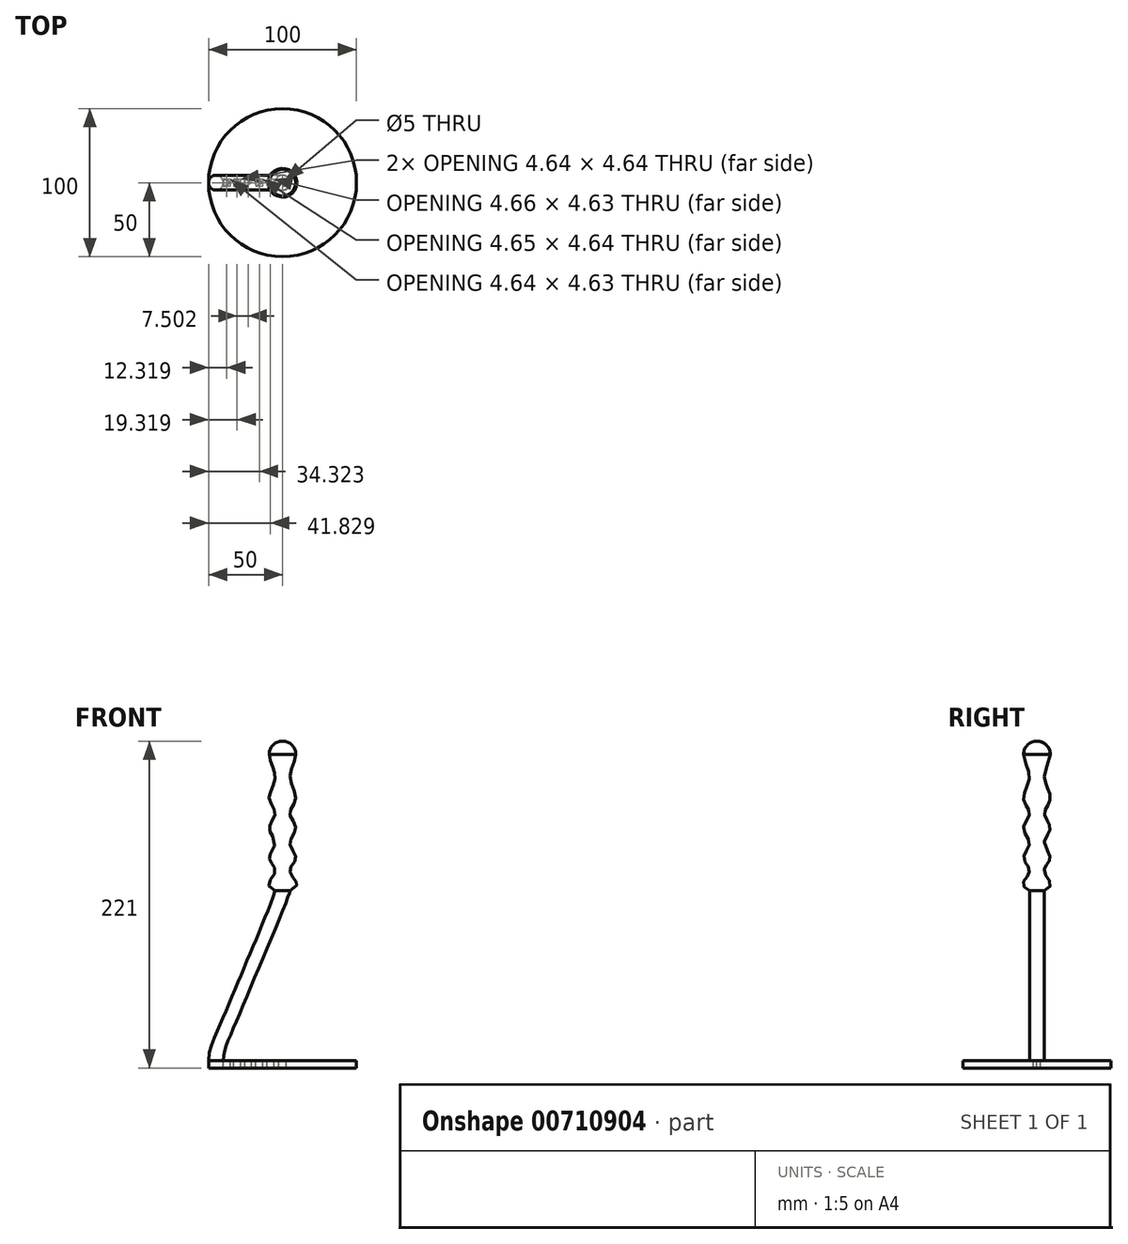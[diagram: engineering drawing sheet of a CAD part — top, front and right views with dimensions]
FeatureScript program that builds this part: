
annotation { "Feature Type Name" : "Feature", "Feature Type Description" : "" }
export const myFeature = defineFeature(function(context is Context, id is Id, definition is map)
    precondition{}
    {
        {
            var Q0;
            Q0=qCreatedBy(makeId("Top.planeOp"),FACE);
            var sketch = newSketch(context, id + "F0", { "sketchPlane" : qUnion([Q0])});
            skCircle(sketch, "E0", {"center": v(0, 0) * mm, "radius": 50 * mm});
            skLineSegment(sketch, "E1", {"start": v(0, 0) * mm, "end": v(-50, 0) * mm, "construction": true});
            skLineSegment(sketch, "E2", {"start": v(-50, 0) * mm, "end": v(-45, 0) * mm, "construction": true});
            skCircle(sketch, "E3", {"center": v(-45, 0) * mm, "radius": 5 * mm});
            skCircle(sketch, "E4", {"center": v(0, 0) * mm, "radius": 40 * mm, "construction": true});
            skLineSegment(sketch, "E5", {"start": v(-39.5, -2.29) * mm, "end": v(-35.53, -0.27) * mm});
            skLineSegment(sketch, "E6", {"start": v(-35.53, 0.27) * mm, "end": v(-39.5, 2.29) * mm});
            skLineSegment(sketch, "E7", {"start": v(-39.94, 2.03) * mm, "end": v(-40, 0) * mm});
            skLineSegment(sketch, "E8", {"start": v(-40, 0) * mm, "end": v(-39.94, -2.03) * mm});
            skPoint(sketch, "E9.visualSharp", {"position": v(-39.92, 2.5) * mm});
            skArc(sketch, "E9.filletArc", {"start": v(-39.5, 2.29) * mm, "mid": v(-39.79, 2.28) * mm, "end": v(-39.94, 2.03) * mm});
            skPoint(sketch, "E10.visualSharp", {"position": v(-35, 0) * mm});
            skArc(sketch, "E10.filletArc", {"start": v(-35.53, -0.27) * mm, "mid": v(-35.36, 0) * mm, "end": v(-35.53, 0.27) * mm});
            skPoint(sketch, "E11.visualSharp", {"position": v(-39.92, -2.5) * mm});
            skArc(sketch, "E11.filletArc", {"start": v(-39.94, -2.03) * mm, "mid": v(-39.79, -2.28) * mm, "end": v(-39.5, -2.29) * mm});
            skLineSegment(sketch, "E12", {"start": v(-35, 0) * mm, "end": v(-33, 0) * mm, "construction": true});
            skCircle(sketch, "E13", {"center": v(0, 0) * mm, "radius": 33 * mm, "construction": true});
            skLineSegment(sketch, "E14", {"start": v(-33, 0) * mm, "end": v(-32.92, 2.03) * mm});
            skLineSegment(sketch, "E15", {"start": v(-32.49, 2.29) * mm, "end": v(-28.52, 0.27) * mm});
            skLineSegment(sketch, "E16", {"start": v(-28.52, -0.27) * mm, "end": v(-32.49, -2.29) * mm});
            skLineSegment(sketch, "E17", {"start": v(-32.92, -2.03) * mm, "end": v(-33, 0) * mm});
            skPoint(sketch, "E18.visualSharp", {"position": v(-28, 0) * mm});
            skArc(sketch, "E18.filletArc", {"start": v(-28.52, -0.27) * mm, "mid": v(-28.36, 0) * mm, "end": v(-28.52, 0.27) * mm});
            skPoint(sketch, "E19.visualSharp", {"position": v(-32.9, 2.5) * mm});
            skArc(sketch, "E19.filletArc", {"start": v(-32.49, 2.29) * mm, "mid": v(-32.78, 2.28) * mm, "end": v(-32.92, 2.03) * mm});
            skPoint(sketch, "E20.visualSharp", {"position": v(-32.9, -2.5) * mm});
            skArc(sketch, "E20.filletArc", {"start": v(-32.92, -2.03) * mm, "mid": v(-32.78, -2.28) * mm, "end": v(-32.49, -2.29) * mm});
            skLineSegment(sketch, "E21", {"start": v(-28, 0) * mm, "end": v(-25.5, 0) * mm, "construction": true});
            skCircle(sketch, "E22", {"center": v(0, 0) * mm, "radius": 25.5 * mm, "construction": true});
            skLineSegment(sketch, "E23", {"start": v(-25.5, 0) * mm, "end": v(-25.4, -2.03) * mm});
            skLineSegment(sketch, "E24", {"start": v(-24.96, -2.29) * mm, "end": v(-21.02, -0.27) * mm});
            skLineSegment(sketch, "E25", {"start": v(-21.02, 0.27) * mm, "end": v(-24.96, 2.29) * mm});
            skLineSegment(sketch, "E26", {"start": v(-25.4, 2.03) * mm, "end": v(-25.5, 0) * mm});
            skPoint(sketch, "E27.visualSharp", {"position": v(-25.38, -2.5) * mm});
            skArc(sketch, "E27.filletArc", {"start": v(-25.4, -2.03) * mm, "mid": v(-25.25, -2.28) * mm, "end": v(-24.96, -2.29) * mm});
            skPoint(sketch, "E28.visualSharp", {"position": v(-25.38, 2.5) * mm});
            skArc(sketch, "E28.filletArc", {"start": v(-24.96, 2.29) * mm, "mid": v(-25.25, 2.28) * mm, "end": v(-25.4, 2.03) * mm});
            skPoint(sketch, "E29.visualSharp", {"position": v(-20.5, 0) * mm});
            skArc(sketch, "E29.filletArc", {"start": v(-21.02, -0.27) * mm, "mid": v(-20.86, 0) * mm, "end": v(-21.02, 0.27) * mm});
            skLineSegment(sketch, "E30", {"start": v(-20.5, 0) * mm, "end": v(-18, 0) * mm, "construction": true});
            skCircle(sketch, "E31", {"center": v(0, 0) * mm, "radius": 18 * mm, "construction": true});
            skLineSegment(sketch, "E32", {"start": v(-13, 0) * mm, "end": v(-10.5, 0) * mm, "construction": true});
            skCircle(sketch, "E33", {"center": v(0, 0) * mm, "radius": 10.5 * mm, "construction": true});
            skLineSegment(sketch, "E34", {"start": v(-17.42, -2.28) * mm, "end": v(-13.52, -0.27) * mm});
            skLineSegment(sketch, "E35", {"start": v(-17.42, 2.28) * mm, "end": v(-13.52, 0.27) * mm});
            skLineSegment(sketch, "E36", {"start": v(-17.86, 2.04) * mm, "end": v(-18, 0) * mm});
            skLineSegment(sketch, "E37", {"start": v(-18, 0) * mm, "end": v(-17.86, -2.04) * mm});
            skPoint(sketch, "E38.visualSharp", {"position": v(-17.83, -2.5) * mm});
            skArc(sketch, "E38.filletArc", {"start": v(-17.86, -2.04) * mm, "mid": v(-17.7, -2.28) * mm, "end": v(-17.42, -2.28) * mm});
            skPoint(sketch, "E39.visualSharp", {"position": v(-17.83, 2.5) * mm});
            skArc(sketch, "E39.filletArc", {"start": v(-17.42, 2.28) * mm, "mid": v(-17.7, 2.28) * mm, "end": v(-17.86, 2.04) * mm});
            skPoint(sketch, "E40.visualSharp", {"position": v(-13, 0) * mm});
            skArc(sketch, "E40.filletArc", {"start": v(-13.52, -0.27) * mm, "mid": v(-13.35, 0) * mm, "end": v(-13.52, 0.27) * mm});
            skLineSegment(sketch, "E41", {"start": v(-10.5, 0) * mm, "end": v(-10.25, -2.05) * mm});
            skLineSegment(sketch, "E42", {"start": v(-9.82, -2.28) * mm, "end": v(-6, -0.27) * mm});
            skLineSegment(sketch, "E43", {"start": v(-6, 0.27) * mm, "end": v(-9.82, 2.28) * mm});
            skLineSegment(sketch, "E44", {"start": v(-10.25, 2.05) * mm, "end": v(-10.5, 0) * mm});
            skPoint(sketch, "E45.visualSharp", {"position": v(-10.2, -2.48) * mm});
            skArc(sketch, "E45.filletArc", {"start": v(-10.25, -2.05) * mm, "mid": v(-10.1, -2.28) * mm, "end": v(-9.82, -2.28) * mm});
            skPoint(sketch, "E46.visualSharp", {"position": v(-10.2, 2.48) * mm});
            skArc(sketch, "E46.filletArc", {"start": v(-9.82, 2.28) * mm, "mid": v(-10.1, 2.28) * mm, "end": v(-10.25, 2.05) * mm});
            skPoint(sketch, "E47.visualSharp", {"position": v(-5.5, 0) * mm});
            skArc(sketch, "E47.filletArc", {"start": v(-6, -0.27) * mm, "mid": v(-5.84, 0) * mm, "end": v(-6, 0.27) * mm});
            skCircle(sketch, "E48", {"center": v(0, 0) * mm, "radius": 2.5 * mm});
            skSolve(sketch);
        }
        {
            var Q0;
            Q0=qCreatedBy(makeId("Front.planeOp"),FACE);
            var sketch = newSketch(context, id + "F1", { "sketchPlane" : qUnion([Q0])});
            skLineSegment(sketch, "E49", {"start": v(0, 0) * mm, "end": v(0, 139) * mm, "construction": true});
            skLineSegment(sketch, "E50.0", {"start": v(-50, 0) * mm, "end": v(-45, 0) * mm, "construction": true});
            skFitSpline(sketch, "E51", {"points": [v(-45, 0) * mm, v(-39, 20) * mm, v(-15, 77) * mm, v(0, 115) * mm], "startDerivative": vector(0, 77.92) * mm, "endDerivative": vector(0, 20.16) * mm});
            skSolve(sketch);
        }
        {
            var Q0;
            {var subQ4=sQuery(id+"F0.wireOp",EDGE,"E0");Q0=makeQuery(id+"F0.imprint","IMPRINT",FACE,{"disambiguationData":[TD([[makeQuery(id+"F0.imprint","IMPRINT",EDGE,{"derivedFrom":subQ4}),1.0]])]});}
            var Q1;
            {var subQ0=sQuery(id+"F0.wireOp",EDGE,"E3");var subQ2=makeQuery(id+"F0.imprint","INTERSECT",VERTEX,{"derivedFrom":[sQuery(id+"F0.wireOp",EDGE,"E0"),subQ0]});Q1=makeQuery(id+"F0.imprint","IMPRINT",FACE,{"disambiguationData":[TD([[makeQuery(id+"F0.imprint","IMPRINT",EDGE,{"disambiguationData":[TD([[subQ2,1.0]])],"derivedFrom":subQ0}),1.0]])]});}
            var Q2;
            Q2=makeQuery(id+"F0.imprint","IMPRINT",FACE,{"disambiguationData":[TD([[makeQuery(id+"F0.imprint","IMPRINT",EDGE,{"derivedFrom":sQuery(id+"F0.wireOp",EDGE,"E5")}),1.0]])]});
            var Q3;
            Q3=makeQuery(id+"F0.imprint","IMPRINT",FACE,{"disambiguationData":[TD([[makeQuery(id+"F0.imprint","IMPRINT",EDGE,{"derivedFrom":sQuery(id+"F0.wireOp",EDGE,"E14")}),-1.0]])]});
            var Q4;
            Q4=makeQuery(id+"F0.imprint","IMPRINT",FACE,{"disambiguationData":[TD([[makeQuery(id+"F0.imprint","IMPRINT",EDGE,{"derivedFrom":sQuery(id+"F0.wireOp",EDGE,"E23")}),1.0]])]});
            var Q5;
            Q5=makeQuery(id+"F0.imprint","IMPRINT",FACE,{"disambiguationData":[TD([[makeQuery(id+"F0.imprint","IMPRINT",EDGE,{"derivedFrom":sQuery(id+"F0.wireOp",EDGE,"E34")}),1.0]])]});
            var Q6;
            Q6=makeQuery(id+"F0.imprint","IMPRINT",FACE,{"disambiguationData":[TD([[makeQuery(id+"F0.imprint","IMPRINT",EDGE,{"derivedFrom":sQuery(id+"F0.wireOp",EDGE,"E41")}),1.0]])]});
            extrude(context, id + "F2", {"entities" : qUnion([Q0, Q1, Q2, Q3, Q4, Q5, Q6]), "oppositeDirection" : true, "depth" : 5 * mm, "offsetDistance" : 25 * mm});
        }
        {
            var Q0;
            Q0=makeQuery(id+"F0.imprint","IMPRINT",FACE,{"disambiguationData":[TD([[makeQuery(id+"F0.imprint","IMPRINT",EDGE,{"derivedFrom":sQuery(id+"F0.wireOp",EDGE,"E5")}),1.0]])]});
            extrude(context, id + "F3", {"entities" : qUnion([Q0]), "operationType" : NewBodyOperationType.REMOVE, "endBound" : BoundingType.THROUGH_ALL, "oppositeDirection" : true, "depth" : 25 * mm, "offsetDistance" : 25 * mm});
        }
        {
            var Q0;
            Q0=makeQuery(id+"F0.imprint","IMPRINT",FACE,{"disambiguationData":[TD([[makeQuery(id+"F0.imprint","IMPRINT",EDGE,{"derivedFrom":sQuery(id+"F0.wireOp",EDGE,"E14")}),-1.0]])]});
            extrude(context, id + "F4", {"entities" : qUnion([Q0]), "operationType" : NewBodyOperationType.REMOVE, "endBound" : BoundingType.UP_TO_NEXT, "oppositeDirection" : true, "depth" : 25 * mm, "offsetDistance" : 25 * mm});
        }
        {
            var Q0;
            Q0=makeQuery(id+"F0.imprint","IMPRINT",FACE,{"disambiguationData":[TD([[makeQuery(id+"F0.imprint","IMPRINT",EDGE,{"derivedFrom":sQuery(id+"F0.wireOp",EDGE,"E23")}),1.0]])]});
            extrude(context, id + "F5", {"entities" : qUnion([Q0]), "operationType" : NewBodyOperationType.REMOVE, "endBound" : BoundingType.UP_TO_NEXT, "oppositeDirection" : true, "depth" : 25 * mm, "offsetDistance" : 25 * mm});
        }
        {
            var Q0;
            Q0=makeQuery(id+"F0.imprint","IMPRINT",FACE,{"disambiguationData":[TD([[makeQuery(id+"F0.imprint","IMPRINT",EDGE,{"derivedFrom":sQuery(id+"F0.wireOp",EDGE,"E34")}),1.0]])]});
            extrude(context, id + "F6", {"entities" : qUnion([Q0]), "operationType" : NewBodyOperationType.REMOVE, "endBound" : BoundingType.UP_TO_NEXT, "oppositeDirection" : true, "depth" : 25 * mm, "offsetDistance" : 25 * mm});
        }
        {
            var Q0;
            Q0=makeQuery(id+"F0.imprint","IMPRINT",FACE,{"disambiguationData":[TD([[makeQuery(id+"F0.imprint","IMPRINT",EDGE,{"derivedFrom":sQuery(id+"F0.wireOp",EDGE,"E41")}),1.0]])]});
            extrude(context, id + "F7", {"entities" : qUnion([Q0]), "operationType" : NewBodyOperationType.REMOVE, "endBound" : BoundingType.UP_TO_NEXT, "oppositeDirection" : true, "depth" : 25 * mm, "offsetDistance" : 25 * mm});
        }
        {
            var Q0;
            {var subQ0=sQuery(id+"F0.wireOp",EDGE,"E3");var subQ2=makeQuery(id+"F0.imprint","INTERSECT",VERTEX,{"derivedFrom":[sQuery(id+"F0.wireOp",EDGE,"E0"),subQ0]});Q0=makeQuery(id+"F0.imprint","IMPRINT",FACE,{"disambiguationData":[TD([[makeQuery(id+"F0.imprint","IMPRINT",EDGE,{"disambiguationData":[TD([[subQ2,1.0]])],"derivedFrom":subQ0}),1.0]])]});}
            var Q1;
            Q1=sQuery(id+"F1.wireOp",EDGE,"E51");
            sweep(context, id + "F8", {"operationType" : NewBodyOperationType.ADD, "profiles" : qUnion([Q0]), "path" : qUnion([Q1]), "keepProfileOrientation" : true});
        }
        {
            var Q0;
            Q0=makeQuery(id+"F8.opSweep","CAP_FACE",FACE,{"disambiguationData":[OSD([sQuery(id+"F0.wireOp",EDGE,"E3"),sQuery(id+"F1.wireOp",VERTEX,"E51.end")])],"isStart":false});
            var sketch = newSketch(context, id + "F9", { "sketchPlane" : qUnion([Q0])});
            skLineSegment(sketch, "E52", {"start": v(0, 0) * mm, "end": v(0, 5) * mm, "construction": true});
            skSolve(sketch);
        }
        {
            var Q0;
            Q0=qCreatedBy(makeId("Right.planeOp"),FACE);
            var sketch = newSketch(context, id + "F10", { "sketchPlane" : qUnion([Q0])});
            skLineSegment(sketch, "E53.0", {"start": v(0, 115) * mm, "end": v(5, 115) * mm});
            skLineSegment(sketch, "E54", {"start": v(5, 115) * mm, "end": v(5, 195) * mm, "construction": true});
            skLineSegment(sketch, "E55", {"start": v(9, 115) * mm, "end": v(9, 195) * mm, "construction": true});
            skLineSegment(sketch, "E56", {"start": v(9, 115) * mm, "end": v(9, 121) * mm, "construction": true});
            skLineSegment(sketch, "E57", {"start": v(9, 121) * mm, "end": v(5, 121) * mm, "construction": true});
            skLineSegment(sketch, "E58", {"start": v(5, 121) * mm, "end": v(5, 129) * mm, "construction": true});
            skLineSegment(sketch, "E59", {"start": v(5, 129) * mm, "end": v(9, 129) * mm, "construction": true});
            skLineSegment(sketch, "E60", {"start": v(9, 129) * mm, "end": v(9, 137) * mm, "construction": true});
            skLineSegment(sketch, "E61", {"start": v(9, 137) * mm, "end": v(5, 137) * mm, "construction": true});
            skLineSegment(sketch, "E62", {"start": v(5, 115) * mm, "end": v(9, 115) * mm, "construction": true});
            skLineSegment(sketch, "E63", {"start": v(5, 137) * mm, "end": v(5, 147) * mm, "construction": true});
            skLineSegment(sketch, "E64", {"start": v(5, 147) * mm, "end": v(9, 147) * mm, "construction": true});
            skLineSegment(sketch, "E65", {"start": v(9, 147) * mm, "end": v(9, 157) * mm, "construction": true});
            skLineSegment(sketch, "E66", {"start": v(9, 157) * mm, "end": v(5, 157) * mm, "construction": true});
            skLineSegment(sketch, "E67", {"start": v(5, 157) * mm, "end": v(5, 167) * mm, "construction": true});
            skLineSegment(sketch, "E68", {"start": v(5, 167) * mm, "end": v(9, 167) * mm, "construction": true});
            skLineSegment(sketch, "E69", {"start": v(9, 167) * mm, "end": v(9, 177) * mm, "construction": true});
            skLineSegment(sketch, "E70", {"start": v(9, 177) * mm, "end": v(5, 177) * mm, "construction": true});
            skLineSegment(sketch, "E71", {"start": v(5, 177) * mm, "end": v(5, 192) * mm, "construction": true});
            skLineSegment(sketch, "E72", {"start": v(5, 192) * mm, "end": v(9, 192) * mm, "construction": true});
            skLineSegment(sketch, "E73", {"start": v(9, 192) * mm, "end": v(9, 207) * mm, "construction": true});
            skLineSegment(sketch, "E74", {"start": v(9, 207) * mm, "end": v(0, 207) * mm, "construction": true});
            skArc(sketch, "E75", {"start": v(9, 207) * mm, "mid": v(6.36, 213.36) * mm, "end": v(0, 216) * mm});
            skLineSegment(sketch, "E76", {"start": v(0, 115) * mm, "end": v(0, 216) * mm});
            skFitSpline(sketch, "E77", {"points": [v(5, 115) * mm, v(9, 121) * mm, v(5, 129) * mm, v(9, 137) * mm, v(5, 147) * mm, v(9, 157) * mm, v(5, 167) * mm, v(9, 177) * mm, v(5, 192) * mm, v(9, 207) * mm], "startDerivative": vector(179.37, 105.48) * mm, "endDerivative": vector(-1.43, 111.96) * mm});
            skSolve(sketch);
        }
        {
            var Q0;
            Q0=makeQuery(id+"F10.imprint","IMPRINT",FACE,{"disambiguationData":[TD([[makeQuery(id+"F10.imprint","IMPRINT",EDGE,{"derivedFrom":sQuery(id+"F10.wireOp",EDGE,"E53.0")}),1.0]])]});
            var Q1;
            Q1=sQuery(id+"F10.wireOp",EDGE,"E76");
            revolve(context, id + "F11", {"operationType" : NewBodyOperationType.ADD, "surfaceOperationType" : NewSurfaceOperationType.NEW, "entities" : qUnion([Q0]), "axis" : qUnion([Q1]), "revolveType" : RevolveType.FULL});
        }
    });
